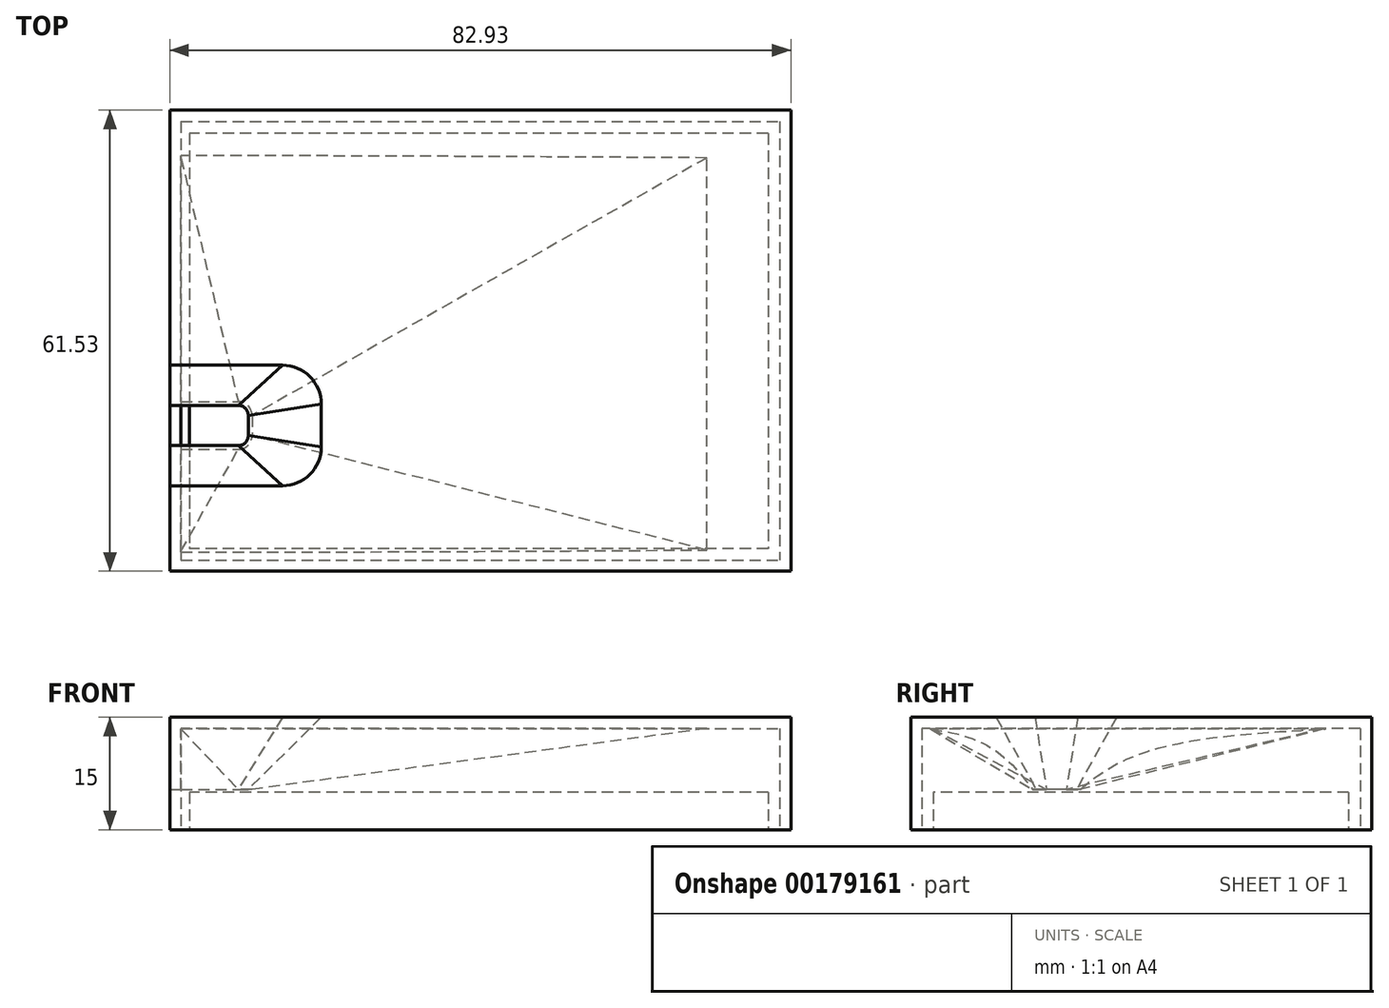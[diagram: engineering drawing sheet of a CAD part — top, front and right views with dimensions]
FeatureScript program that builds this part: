
annotation { "Feature Type Name" : "Feature", "Feature Type Description" : "" }
export const myFeature = defineFeature(function(context is Context, id is Id, definition is map)
    precondition{}
    {
        {
            var Q0;
            Q0=qCreatedBy(makeId("Top.planeOp"),FACE);
            var sketch = newSketch(context, id + "F0", { "sketchPlane" : qUnion([Q0])});
            skLineSegment(sketch, "E0.bottom", {"start": v(-40, 29.3) * mm, "end": v(42.94, 29.3) * mm});
            skLineSegment(sketch, "E0.top", {"start": v(-40, -32.24) * mm, "end": v(42.94, -32.24) * mm});
            skLineSegment(sketch, "E0.left", {"start": v(-40, 29.3) * mm, "end": v(-40, -32.24) * mm});
            skLineSegment(sketch, "E0.right", {"start": v(42.94, 29.3) * mm, "end": v(42.94, -32.24) * mm});
            skSolve(sketch);
        }
        {
            var Q0;
            Q0 = qSketchRegion(id + "F0", true);
            extrude(context, id + "F1", {"entities" : qUnion([Q0]), "flatOperationType" : FlatOperationType.REMOVE, "depth" : 15 * mm, "offsetDistance" : 25 * mm, "domain" : OperationDomain.MODEL});
        }
        {
            var Q0;
            Q0=makeQuery(id+"F1.opExtrude","CAP_FACE",FACE,{"disambiguationData":[OSD([sQuery(id+"F0.wireOp",EDGE,"E0.bottom"),sQuery(id+"F0.wireOp",EDGE,"E0.top"),sQuery(id+"F0.wireOp",EDGE,"E0.left"),sQuery(id+"F0.wireOp",EDGE,"E0.right")])],"isStart":true});
            shell(context, id + "F2", {"entities" : qUnion([Q0]), "thickness" : 1.5 * mm});
        }
        {
            var Q0;
            Q0=qCreatedBy(makeId("Top.planeOp"),FACE);
            var sketch = newSketch(context, id + "F3", { "sketchPlane" : qUnion([Q0])});
            skLineSegment(sketch, "E1.bottom", {"start": v(39.89, 26.2) * mm, "end": v(-37.35, 26.2) * mm});
            skLineSegment(sketch, "E1.top", {"start": v(39.89, -29.23) * mm, "end": v(-37.35, -29.23) * mm});
            skLineSegment(sketch, "E1.left", {"start": v(39.89, 26.2) * mm, "end": v(39.89, -29.23) * mm});
            skLineSegment(sketch, "E1.right", {"start": v(-37.35, 26.2) * mm, "end": v(-37.35, -29.23) * mm});
            skSolve(sketch);
        }
        {
            var Q0;
            Q0 = qSketchRegion(id + "F3", true);
            extrude(context, id + "F4", {"entities" : qUnion([Q0]), "flatOperationType" : FlatOperationType.REMOVE, "depth" : 5 * mm, "offsetDistance" : 25 * mm, "domain" : OperationDomain.MODEL});
        }
        {
            var Q0;
            Q0=makeQuery(id+"F1.opExtrude","CAP_FACE",FACE,{"disambiguationData":[OSD([sQuery(id+"F0.wireOp",EDGE,"E0.bottom"),sQuery(id+"F0.wireOp",EDGE,"E0.top"),sQuery(id+"F0.wireOp",EDGE,"E0.left"),sQuery(id+"F0.wireOp",EDGE,"E0.right")])],"isStart":false});
            cPlane(context, id + "F5", {"entities" : qUnion([Q0]), "cplaneType" : CPlaneType.OFFSET, "offset" : 9.6 * mm, "oppositeDirection" : true, "width" : 150 * mm, "height" : 150 * mm});
        }
        {
            var Q0;
            Q0=makeQuery(id+"F1.opExtrude","CAP_FACE",FACE,{"disambiguationData":[OSD([sQuery(id+"F0.wireOp",EDGE,"E0.bottom"),sQuery(id+"F0.wireOp",EDGE,"E0.top"),sQuery(id+"F0.wireOp",EDGE,"E0.left"),sQuery(id+"F0.wireOp",EDGE,"E0.right")])],"isStart":false});
            var sketch = newSketch(context, id + "F6", { "sketchPlane" : qUnion([Q0])});
            skLineSegment(sketch, "E2", {"start": v(-40, -4.25) * mm, "end": v(-24.96, -4.25) * mm});
            skArc(sketch, "E3", {"start": v(-19.26, -9.95) * mm, "mid": v(-20.93, -5.92) * mm, "end": v(-24.96, -4.25) * mm});
            skLineSegment(sketch, "E4", {"start": v(-40, -12.8) * mm, "end": v(-31.56, -12.8) * mm, "construction": true});
            skArc(sketch, "E5.MirrorC", {"start": v(-19.26, -15.64) * mm, "mid": v(-20.93, -19.67) * mm, "end": v(-24.96, -21.33) * mm});
            skLineSegment(sketch, "E6.MirrorCS", {"start": v(-40, -21.33) * mm, "end": v(-24.96, -21.33) * mm});
            skLineSegment(sketch, "E7", {"start": v(-19.26, -9.95) * mm, "end": v(-19.26, -15.64) * mm});
            skLineSegment(sketch, "E8", {"start": v(-40, -4.25) * mm, "end": v(-40, -21.33) * mm});
            skLineSegment(sketch, "E9.0", {"start": v(-40, -20.83) * mm, "end": v(-24.96, -20.83) * mm});
            skLineSegment(sketch, "E9.1", {"start": v(-40, -4.75) * mm, "end": v(-24.96, -4.75) * mm});
            skArc(sketch, "E9.2", {"start": v(-19.76, -9.95) * mm, "mid": v(-21.28, -6.27) * mm, "end": v(-24.96, -4.75) * mm});
            skLineSegment(sketch, "E9.3", {"start": v(-19.76, -9.95) * mm, "end": v(-19.76, -15.64) * mm});
            skArc(sketch, "E9.4", {"start": v(-19.76, -15.64) * mm, "mid": v(-21.28, -19.31) * mm, "end": v(-24.96, -20.83) * mm});
            skSolve(sketch);
        }
        {
            var Q0;
            Q0=qCreatedBy(id+"F5.planeOp",FACE);
            var sketch = newSketch(context, id + "F7", { "sketchPlane" : qUnion([Q0])});
            skLineSegment(sketch, "E10", {"start": v(-40, -9.6) * mm, "end": v(-30.86, -9.6) * mm});
            skArc(sketch, "E11", {"start": v(-29, -11.46) * mm, "mid": v(-29.55, -10.14) * mm, "end": v(-30.86, -9.6) * mm});
            skLineSegment(sketch, "E12", {"start": v(-40, -12.8) * mm, "end": v(-32.62, -12.8) * mm, "construction": true});
            skArc(sketch, "E13.MirrorC", {"start": v(-29, -14.13) * mm, "mid": v(-29.55, -15.44) * mm, "end": v(-30.86, -15.98) * mm});
            skLineSegment(sketch, "E14.MirrorCS", {"start": v(-40, -15.98) * mm, "end": v(-30.86, -15.98) * mm});
            skLineSegment(sketch, "E15", {"start": v(-29, -11.46) * mm, "end": v(-29, -14.13) * mm});
            skLineSegment(sketch, "E16", {"start": v(-40, -9.6) * mm, "end": v(-40, -15.98) * mm});
            skLineSegment(sketch, "E17.0", {"start": v(-40, -15.48) * mm, "end": v(-30.86, -15.48) * mm});
            skLineSegment(sketch, "E17.1", {"start": v(-40, -10.1) * mm, "end": v(-30.86, -10.1) * mm});
            skArc(sketch, "E17.2", {"start": v(-29.5, -11.46) * mm, "mid": v(-29.9, -10.5) * mm, "end": v(-30.86, -10.1) * mm});
            skLineSegment(sketch, "E17.3", {"start": v(-29.5, -11.46) * mm, "end": v(-29.5, -14.13) * mm});
            skArc(sketch, "E17.4", {"start": v(-29.5, -14.13) * mm, "mid": v(-29.9, -15.09) * mm, "end": v(-30.86, -15.48) * mm});
            skSolve(sketch);
        }
        {
            var Q0;
            {var subQ4=sQuery(id+"F6.wireOp",EDGE,"E2");Q0=makeQuery(id+"F6.imprint","IMPRINT",FACE,{"disambiguationData":[TD([[makeQuery(id+"F6.imprint","IMPRINT",EDGE,{"derivedFrom":subQ4}),-1.0]])]});}
            var Q1;
            {var subQ0=sQuery(id+"F6.wireOp",EDGE,"E3");var subQ1=makeQuery(id+"F6.imprint","INTERSECT",VERTEX,{"derivedFrom":[sQuery(id+"F6.wireOp",EDGE,"E2"),subQ0]});Q1=makeQuery(id+"F6.imprint","IMPRINT",FACE,{"disambiguationData":[TD([[makeQuery(id+"F6.imprint","IMPRINT",EDGE,{"disambiguationData":[TD([[subQ1,1.0]])],"derivedFrom":subQ0}),1.0]])]});}
            var Q2;
            {var subQ0=sQuery(id+"F6.wireOp",EDGE,"E5.MirrorC");var subQ1=makeQuery(id+"F6.imprint","INTERSECT",VERTEX,{"derivedFrom":[subQ0,sQuery(id+"F6.wireOp",EDGE,"E6.MirrorCS")]});Q2=makeQuery(id+"F6.imprint","IMPRINT",FACE,{"disambiguationData":[TD([[makeQuery(id+"F6.imprint","IMPRINT",EDGE,{"disambiguationData":[TD([[subQ1,1.0]])],"derivedFrom":subQ0}),-1.0]])]});}
            var Q3;
            {var subQ1=sQuery(id+"F6.wireOp",EDGE,"E9.0");Q3=makeQuery(id+"F6.imprint","IMPRINT",FACE,{"disambiguationData":[TD([[makeQuery(id+"F6.imprint","IMPRINT",EDGE,{"derivedFrom":subQ1}),1.0]])]});}
            var Q4;
            {var subQ4=sQuery(id+"F7.wireOp",EDGE,"E10");Q4=makeQuery(id+"F7.imprint","IMPRINT",FACE,{"disambiguationData":[TD([[makeQuery(id+"F7.imprint","IMPRINT",EDGE,{"derivedFrom":subQ4}),-1.0]])]});}
            var Q5;
            {var subQ0=sQuery(id+"F7.wireOp",EDGE,"E11");var subQ1=makeQuery(id+"F7.imprint","INTERSECT",VERTEX,{"derivedFrom":[sQuery(id+"F7.wireOp",EDGE,"E10"),subQ0]});Q5=makeQuery(id+"F7.imprint","IMPRINT",FACE,{"disambiguationData":[TD([[makeQuery(id+"F7.imprint","IMPRINT",EDGE,{"disambiguationData":[TD([[subQ1,1.0]])],"derivedFrom":subQ0}),1.0]])]});}
            var Q6;
            {var subQ0=sQuery(id+"F7.wireOp",EDGE,"E13.MirrorC");var subQ1=makeQuery(id+"F7.imprint","INTERSECT",VERTEX,{"derivedFrom":[subQ0,sQuery(id+"F7.wireOp",EDGE,"E14.MirrorCS")]});Q6=makeQuery(id+"F7.imprint","IMPRINT",FACE,{"disambiguationData":[TD([[makeQuery(id+"F7.imprint","IMPRINT",EDGE,{"disambiguationData":[TD([[subQ1,1.0]])],"derivedFrom":subQ0}),-1.0]])]});}
            var Q7;
            {var subQ1=sQuery(id+"F7.wireOp",EDGE,"E17.0");Q7=makeQuery(id+"F7.imprint","IMPRINT",FACE,{"disambiguationData":[TD([[makeQuery(id+"F7.imprint","IMPRINT",EDGE,{"derivedFrom":subQ1}),1.0]])]});}
            loft(context, id + "F8", {"operationType" : NewBodyOperationType.ADD, "sheetProfilesArray" : [{ "sheetProfileEntities" : qUnion([Q0, Q1, Q2, Q3]) }, { "sheetProfileEntities" : qUnion([Q4, Q5, Q6, Q7]) }], "trimGuidesByProfiles" : true});
        }
        {
            var Q0;
            {var subQ1=sQuery(id+"F6.wireOp",EDGE,"E9.0");Q0=makeQuery(id+"F6.imprint","IMPRINT",FACE,{"disambiguationData":[TD([[makeQuery(id+"F6.imprint","IMPRINT",EDGE,{"derivedFrom":subQ1}),1.0]])]});}
            var Q1;
            {var subQ1=sQuery(id+"F7.wireOp",EDGE,"E17.0");Q1=makeQuery(id+"F7.imprint","IMPRINT",FACE,{"disambiguationData":[TD([[makeQuery(id+"F7.imprint","IMPRINT",EDGE,{"derivedFrom":subQ1}),1.0]])]});}
            loft(context, id + "F9", {"operationType" : NewBodyOperationType.REMOVE, "sheetProfilesArray" : [{ "sheetProfileEntities" : qUnion([Q0]) }, { "sheetProfileEntities" : qUnion([Q1]) }]});
        }
    });
